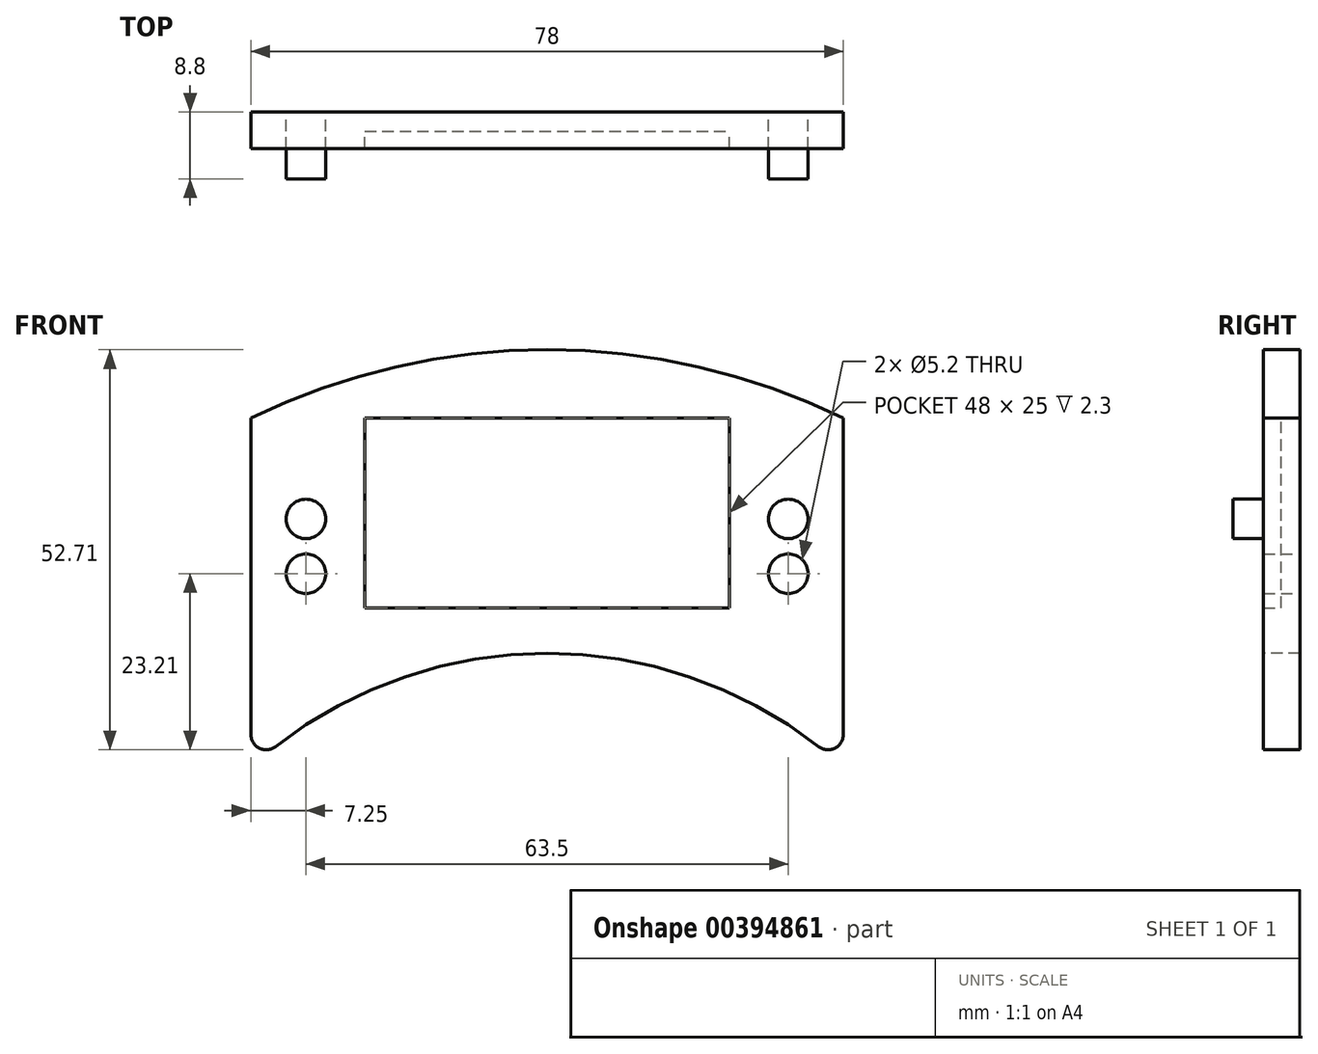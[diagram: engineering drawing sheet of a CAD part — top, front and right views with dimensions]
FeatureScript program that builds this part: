
annotation { "Feature Type Name" : "Feature", "Feature Type Description" : "" }
export const myFeature = defineFeature(function(context is Context, id is Id, definition is map)
    precondition{}
    {
        {
            var Q0;
            Q0=qCreatedBy(makeId("Front.planeOp"),FACE);
            var sketch = newSketch(context, id + "F0", { "sketchPlane" : qUnion([Q0])});
            skLineSegment(sketch, "E0", {"start": v(-39, -46) * mm, "end": v(-39, 0) * mm});
            skLineSegment(sketch, "E1", {"start": v(-39, 0) * mm, "end": v(39, 0) * mm, "construction": true});
            skLineSegment(sketch, "E2", {"start": v(39, 0) * mm, "end": v(39, -46) * mm});
            skArc(sketch, "E3", {"start": v(39, -46) * mm, "mid": v(0, -31) * mm, "end": v(-39, -46) * mm});
            skArc(sketch, "E4", {"start": v(39, 0) * mm, "mid": v(0, 9) * mm, "end": v(-39, 0) * mm});
            skSolve(sketch);
        }
        {
            var Q0;
            Q0=qSketchRegion(id+"F0",true);
            extrude(context, id + "F1", {"entities" : qUnion([Q0]), "oppositeDirection" : true, "depth" : 4.8 * mm});
        }
        {
            var Q0;
            Q0=makeQuery(id+"F1.opExtrude","CAP_FACE",FACE,{"disambiguationData":[OSD([sQuery(id+"F0.wireOp",EDGE,"E0"),sQuery(id+"F0.wireOp",EDGE,"E2"),sQuery(id+"F0.wireOp",EDGE,"E3"),sQuery(id+"F0.wireOp",EDGE,"E4")])],"isStart":true});
            var sketch = newSketch(context, id + "F2", { "sketchPlane" : qUnion([Q0])});
            skCircle(sketch, "E5", {"center": v(-31.75, -20.5) * mm, "radius": 2.6 * mm, "construction": true});
            skCircle(sketch, "E6", {"center": v(31.75, -20.5) * mm, "radius": 2.6 * mm, "construction": true});
            skCircle(sketch, "E7", {"center": v(-31.75, -13.3) * mm, "radius": 2.6 * mm});
            skCircle(sketch, "E8.MirrorC", {"center": v(31.75, -13.3) * mm, "radius": 2.6 * mm});
            skSolve(sketch);
        }
        {
            var Q0;
            Q0=qSketchRegion(id+"F2",true);
            extrude(context, id + "F3", {"entities" : qUnion([Q0]), "operationType" : NewBodyOperationType.ADD, "depth" : 4 * mm});
        }
        {
            var Q0;
            Q0=makeQuery(id+"F1.opExtrude","CAP_FACE",FACE,{"disambiguationData":[OSD([sQuery(id+"F0.wireOp",EDGE,"E0"),sQuery(id+"F0.wireOp",EDGE,"E2"),sQuery(id+"F0.wireOp",EDGE,"E3"),sQuery(id+"F0.wireOp",EDGE,"E4")])],"isStart":false});
            var sketch = newSketch(context, id + "F4", { "sketchPlane" : qUnion([Q0])});
            skPoint(sketch, "E9", {"position": v(-31.75, -20.5) * mm});
            skCircle(sketch, "E10", {"center": v(-31.75, -20.5) * mm, "radius": 2.6 * mm});
            skCircle(sketch, "E11", {"center": v(-31.75, -13.3) * mm, "radius": 2.6 * mm, "construction": true});
            skCircle(sketch, "E12.MirrorC", {"center": v(31.75, -20.5) * mm, "radius": 2.6 * mm});
            skSolve(sketch);
        }
        {
            var Q0;
            Q0=qSketchRegion(id+"F4",true);
            extrude(context, id + "F5", {"entities" : qUnion([Q0]), "operationType" : NewBodyOperationType.REMOVE, "endBound" : BoundingType.UP_TO_NEXT, "oppositeDirection" : true, "depth" : 2.2 * mm});
        }
        {
            var Q0;
            Q0=makeQuery(id+"F1.opExtrude","SWEPT_EDGE",EDGE,{"disambiguationData":[OSD([sQuery(id+"F0.wireOp",EDGE,"E0"),sQuery(id+"F0.wireOp",EDGE,"E3")])]});
            var Q1;
            Q1=makeQuery(id+"F1.opExtrude","SWEPT_EDGE",EDGE,{"disambiguationData":[OSD([sQuery(id+"F0.wireOp",EDGE,"E2"),sQuery(id+"F0.wireOp",EDGE,"E3")])]});
            fillet(context, id + "F6", {"entities" : qUnion([Q0, Q1]), "radius" : 2 * mm, "tangentPropagation" : true, "allowEdgeOverflow" : false});
        }
        {
            var Q0;
            Q0=qCreatedBy(makeId("Top.planeOp"),FACE);
            var sketch = newSketch(context, id + "F7", { "sketchPlane" : qUnion([Q0])});
            skLineSegment(sketch, "E13.bottom", {"start": v(-24, 0) * mm, "end": v(24, 0) * mm});
            skLineSegment(sketch, "E13.top", {"start": v(-24, 2.3) * mm, "end": v(24, 2.3) * mm});
            skLineSegment(sketch, "E13.left", {"start": v(-24, 0) * mm, "end": v(-24, 2.3) * mm});
            skLineSegment(sketch, "E13.right", {"start": v(24, 0) * mm, "end": v(24, 2.3) * mm});
            skSolve(sketch);
        }
        {
            var Q0;
            Q0=qSketchRegion(id+"F7",true);
            extrude(context, id + "F8", {"entities" : qUnion([Q0]), "operationType" : NewBodyOperationType.REMOVE, "oppositeDirection" : true, "depth" : 25 * mm});
        }
    });
